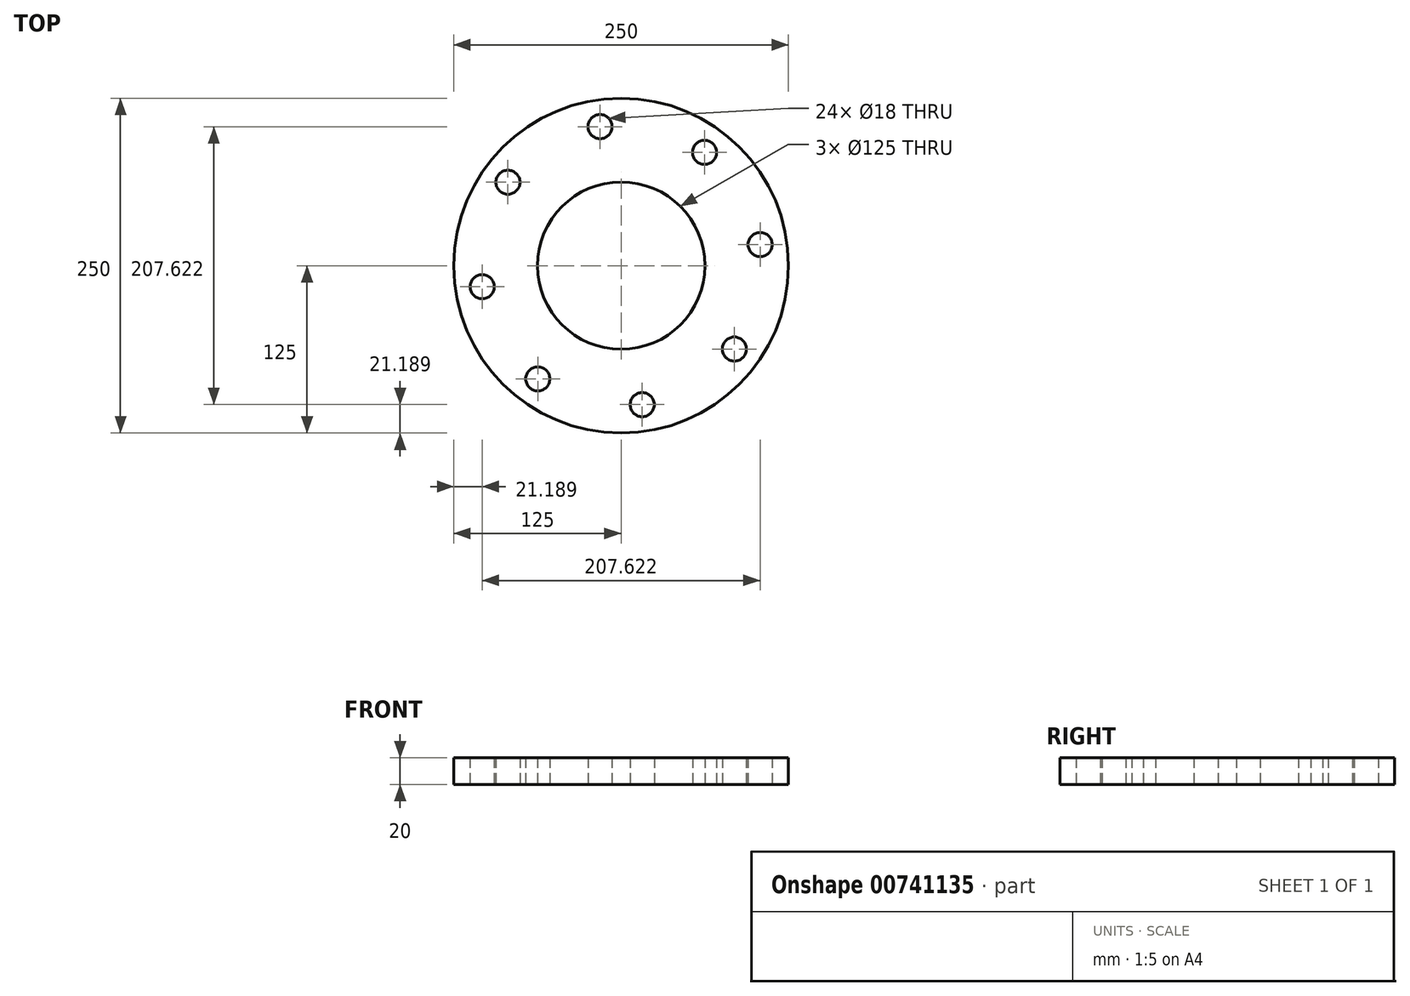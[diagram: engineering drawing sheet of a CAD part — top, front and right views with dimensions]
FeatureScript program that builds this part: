
annotation { "Feature Type Name" : "Feature", "Feature Type Description" : "" }
export const myFeature = defineFeature(function(context is Context, id is Id, definition is map)
    precondition{}
    {
        {
            var Q0;
            Q0=qCreatedBy(makeId("Top.planeOp"),FACE);
            var sketch = newSketch(context, id + "F0", { "sketchPlane" : qUnion([Q0])});
            skCircle(sketch, "E0", {"center": v(0, 0) * mm, "radius": 62.5 * mm});
            skCircle(sketch, "E1", {"center": v(0, 0) * mm, "radius": 105 * mm, "construction": true});
            skCircle(sketch, "E2", {"center": v(0, 0) * mm, "radius": 125 * mm});
            skCircle(sketch, "E3", {"center": v(-15.76, 103.81) * mm, "radius": 9 * mm});
            skCircle(sketch, "E4.1.0", {"center": v(-84.55, 62.26) * mm, "radius": 9 * mm});
            skCircle(sketch, "E4.2.0", {"center": v(-103.81, -15.76) * mm, "radius": 9 * mm});
            skCircle(sketch, "E4.3.0", {"center": v(-62.26, -84.55) * mm, "radius": 9 * mm});
            skCircle(sketch, "E4.4.0", {"center": v(15.76, -103.81) * mm, "radius": 9 * mm});
            skCircle(sketch, "E4.5.0", {"center": v(84.55, -62.26) * mm, "radius": 9 * mm});
            skCircle(sketch, "E4.6.0", {"center": v(103.81, 15.76) * mm, "radius": 9 * mm});
            skCircle(sketch, "E4.7.0", {"center": v(62.26, 84.55) * mm, "radius": 9 * mm});
            skSolve(sketch);
        }
        {
            var Q0;
            Q0=makeQuery(id+"F0.imprint","IMPRINT",FACE,{"disambiguationData":[TD([[makeQuery(id+"F0.imprint","IMPRINT",EDGE,{"derivedFrom":sQuery(id+"F0.wireOp",EDGE,"E0")}),-1.0]])]});
            extrude(context, id + "F1", {"entities" : qUnion([Q0]), "depth" : 20 * mm, "offsetDistance" : 25 * mm});
        }
    });
